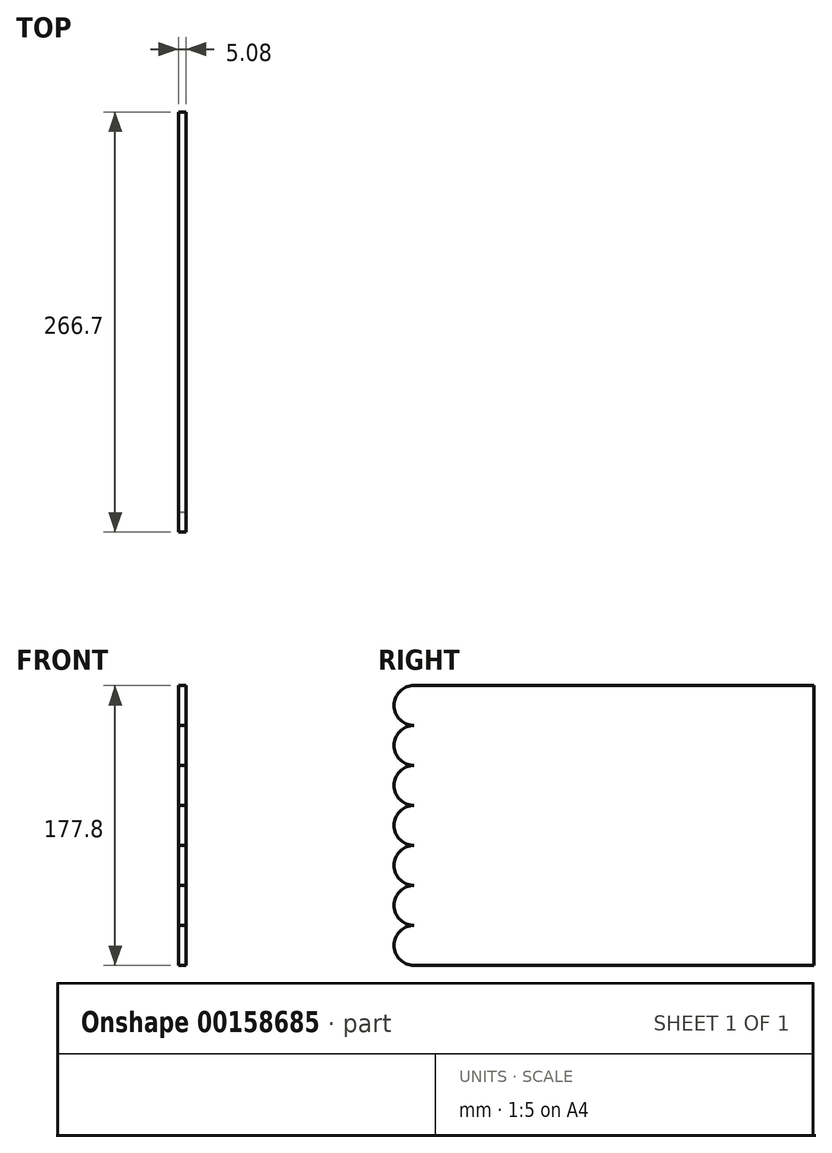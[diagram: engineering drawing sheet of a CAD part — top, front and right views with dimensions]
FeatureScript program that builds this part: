
annotation { "Feature Type Name" : "Feature", "Feature Type Description" : "" }
export const myFeature = defineFeature(function(context is Context, id is Id, definition is map)
    precondition{}
    {
        {
            var Q0;
            Q0=qCreatedBy(makeId("Right.planeOp"),FACE);
            var sketch = newSketch(context, id + "F0", { "sketchPlane" : qUnion([Q0])});
            skLineSegment(sketch, "E0.bottom", {"start": v(-89.25, 95.78) * mm, "end": v(164.75, 95.78) * mm});
            skLineSegment(sketch, "E0.top", {"start": v(-89.25, -82.02) * mm, "end": v(164.75, -82.02) * mm});
            skLineSegment(sketch, "E0.left", {"start": v(-89.25, 95.78) * mm, "end": v(-89.25, -82.02) * mm});
            skLineSegment(sketch, "E0.right", {"start": v(164.75, 95.78) * mm, "end": v(164.75, -82.02) * mm});
            skSolve(sketch);
        }
        {
            var Q0;
            Q0 = qSketchRegion(id + "F0", true);
            extrude(context, id + "F1", {"entities" : qUnion([Q0]), "depth" : 5.08 * mm});
        }
        {
            var Q0;
            Q0=makeQuery(id+"F1.opExtrude","CAP_FACE",FACE,{"disambiguationData":[OSD([sQuery(id+"F0.wireOp",EDGE,"E0.bottom"),sQuery(id+"F0.wireOp",EDGE,"E0.top"),sQuery(id+"F0.wireOp",EDGE,"E0.left"),sQuery(id+"F0.wireOp",EDGE,"E0.right")])],"isStart":false});
            var sketch = newSketch(context, id + "F2", { "sketchPlane" : qUnion([Q0])});
            skText(sketch, "E1", { "text": "I Love My\n            \n\n          \n          Rapids Dog!\n", "fontName": "RobotoSlab-Bold.ttf"});
            skArc(sketch, "E2", {"start": v(-89.25, 95.78) * mm, "mid": v(-101.95, 83.08) * mm, "end": v(-89.25, 70.38) * mm});
            skArc(sketch, "E3", {"start": v(-89.25, 70.38) * mm, "mid": v(-101.95, 57.68) * mm, "end": v(-89.25, 44.98) * mm});
            skArc(sketch, "E4", {"start": v(-89.25, 44.98) * mm, "mid": v(-101.95, 32.28) * mm, "end": v(-89.25, 19.58) * mm});
            skArc(sketch, "E5", {"start": v(-89.25, 19.58) * mm, "mid": v(-101.95, 6.88) * mm, "end": v(-89.25, -5.82) * mm});
            skArc(sketch, "E6", {"start": v(-89.25, -5.82) * mm, "mid": v(-101.95, -18.52) * mm, "end": v(-89.25, -31.22) * mm});
            skArc(sketch, "E7", {"start": v(-89.25, -31.22) * mm, "mid": v(-101.95, -43.92) * mm, "end": v(-89.25, -56.62) * mm});
            skArc(sketch, "E8", {"start": v(-89.25, -56.62) * mm, "mid": v(-101.95, -69.32) * mm, "end": v(-89.25, -82.02) * mm});
            const initialGuessF2  = {"E1": [-0.06702, 0.07133, 1, 0, 0.01874]};
            skSetInitialGuess(sketch, initialGuessF2);
            skSolve(sketch);
        }
        {
            var Q0;
            {var subQ0=sQuery(id+"F2.wireOp",EDGE,"E2");Q0=makeQuery(id+"F2.imprint","IMPRINT",FACE,{"disambiguationData":[TD([[makeQuery(id+"F2.imprint","IMPRINT",EDGE,{"derivedFrom":subQ0}),1.0]])]});}
            var Q1;
            {var subQ0=sQuery(id+"F2.wireOp",EDGE,"E3");Q1=makeQuery(id+"F2.imprint","IMPRINT",FACE,{"disambiguationData":[TD([[makeQuery(id+"F2.imprint","IMPRINT",EDGE,{"derivedFrom":subQ0}),1.0]])]});}
            var Q2;
            {var subQ0=sQuery(id+"F2.wireOp",EDGE,"E4");Q2=makeQuery(id+"F2.imprint","IMPRINT",FACE,{"disambiguationData":[TD([[makeQuery(id+"F2.imprint","IMPRINT",EDGE,{"derivedFrom":subQ0}),1.0]])]});}
            var Q3;
            {var subQ0=sQuery(id+"F2.wireOp",EDGE,"E5");Q3=makeQuery(id+"F2.imprint","IMPRINT",FACE,{"disambiguationData":[TD([[makeQuery(id+"F2.imprint","IMPRINT",EDGE,{"derivedFrom":subQ0}),1.0]])]});}
            var Q4;
            {var subQ0=sQuery(id+"F2.wireOp",EDGE,"E6");Q4=makeQuery(id+"F2.imprint","IMPRINT",FACE,{"disambiguationData":[TD([[makeQuery(id+"F2.imprint","IMPRINT",EDGE,{"derivedFrom":subQ0}),1.0]])]});}
            var Q5;
            {var subQ0=sQuery(id+"F2.wireOp",EDGE,"E7");Q5=makeQuery(id+"F2.imprint","IMPRINT",FACE,{"disambiguationData":[TD([[makeQuery(id+"F2.imprint","IMPRINT",EDGE,{"derivedFrom":subQ0}),1.0]])]});}
            var Q6;
            {var subQ0=sQuery(id+"F2.wireOp",EDGE,"E8");Q6=makeQuery(id+"F2.imprint","IMPRINT",FACE,{"disambiguationData":[TD([[makeQuery(id+"F2.imprint","IMPRINT",EDGE,{"derivedFrom":subQ0}),1.0]])]});}
            extrude(context, id + "F3", {"entities" : qUnion([Q0, Q1, Q2, Q3, Q4, Q5, Q6]), "operationType" : NewBodyOperationType.ADD, "oppositeDirection" : true, "depth" : 5.08 * mm});
        }
    });
